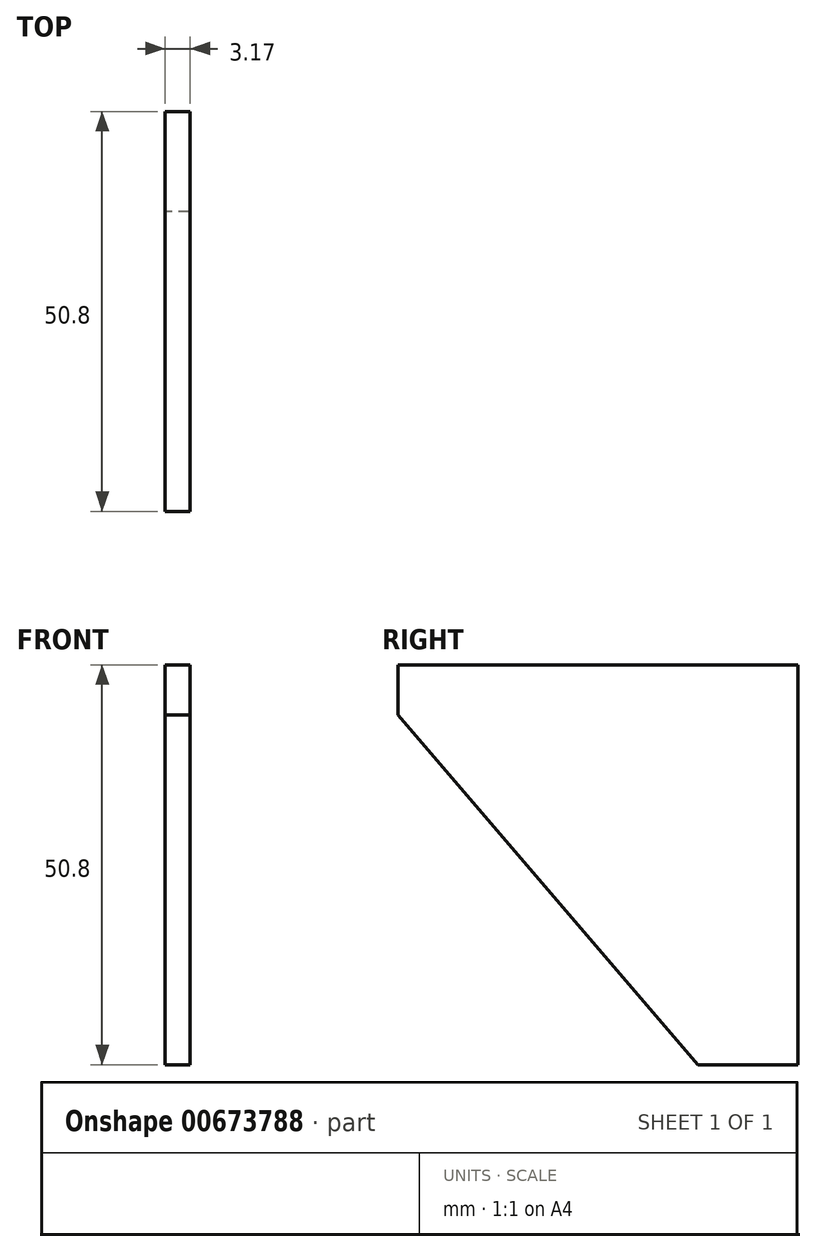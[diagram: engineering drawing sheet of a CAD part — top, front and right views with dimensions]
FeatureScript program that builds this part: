
annotation { "Feature Type Name" : "Feature", "Feature Type Description" : "" }
export const myFeature = defineFeature(function(context is Context, id is Id, definition is map)
    precondition{}
    {
        {
            var Q0;
            Q0=qCreatedBy(makeId("Right.planeOp"),FACE);
            var sketch = newSketch(context, id + "F0", { "sketchPlane" : qUnion([Q0])});
            skLineSegment(sketch, "E0.bottom", {"start": v(25.4, 25.4) * mm, "end": v(-25.4, 25.4) * mm});
            skLineSegment(sketch, "E0.top", {"start": v(25.4, -25.4) * mm, "end": v(12.7, -25.4) * mm});
            skLineSegment(sketch, "E0.left", {"start": v(25.4, 25.4) * mm, "end": v(25.4, -25.4) * mm});
            skLineSegment(sketch, "E0.right", {"start": v(-25.4, 25.4) * mm, "end": v(-25.4, 19.05) * mm});
            skPoint(sketch, "E0.middle", {"position": v(0, 0) * mm});
            skLineSegment(sketch, "E1", {"start": v(12.7, -25.4) * mm, "end": v(-25.4, 19.05) * mm});
            skPoint(sketch, "E2.orphan", {"position": v(-25.4, -25.4) * mm});
            skSolve(sketch);
        }
        {
            var Q0;
            Q0 = qSketchRegion(id + "F0", true);
            extrude(context, id + "F1", {"entities" : qUnion([Q0]), "depth" : 3.17 * mm, "offsetDistance" : 25.4 * mm});
        }
    });
